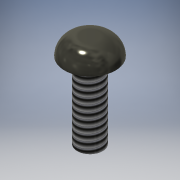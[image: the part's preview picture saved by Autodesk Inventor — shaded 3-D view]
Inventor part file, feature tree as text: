
AUTODESK INVENTOR PART (.ipt)
format: ipt  version: 2016 (Build 200138000, 138)  size: 141,312 bytes
history: native  units: mm
features: sketch x3, extrude x2, other x1, fillet x1, thread x1
ambient origin geometry x1: Origin
bodies: Body1 (feature_tree)
feature tree (8):
  other  "ソリッド1"
  extrude  "押し出し1"  Depth=2.0mm
  extrude  "押し出し2"  Depth=6.0mm TaperAngle=0.0deg
  fillet  "フィレット1"  Radius=4.0mm
  thread  "ねじ1"
  sketch  "スケッチ3"
  sketch  "スケッチ1"
  sketch  "スケッチ2"
